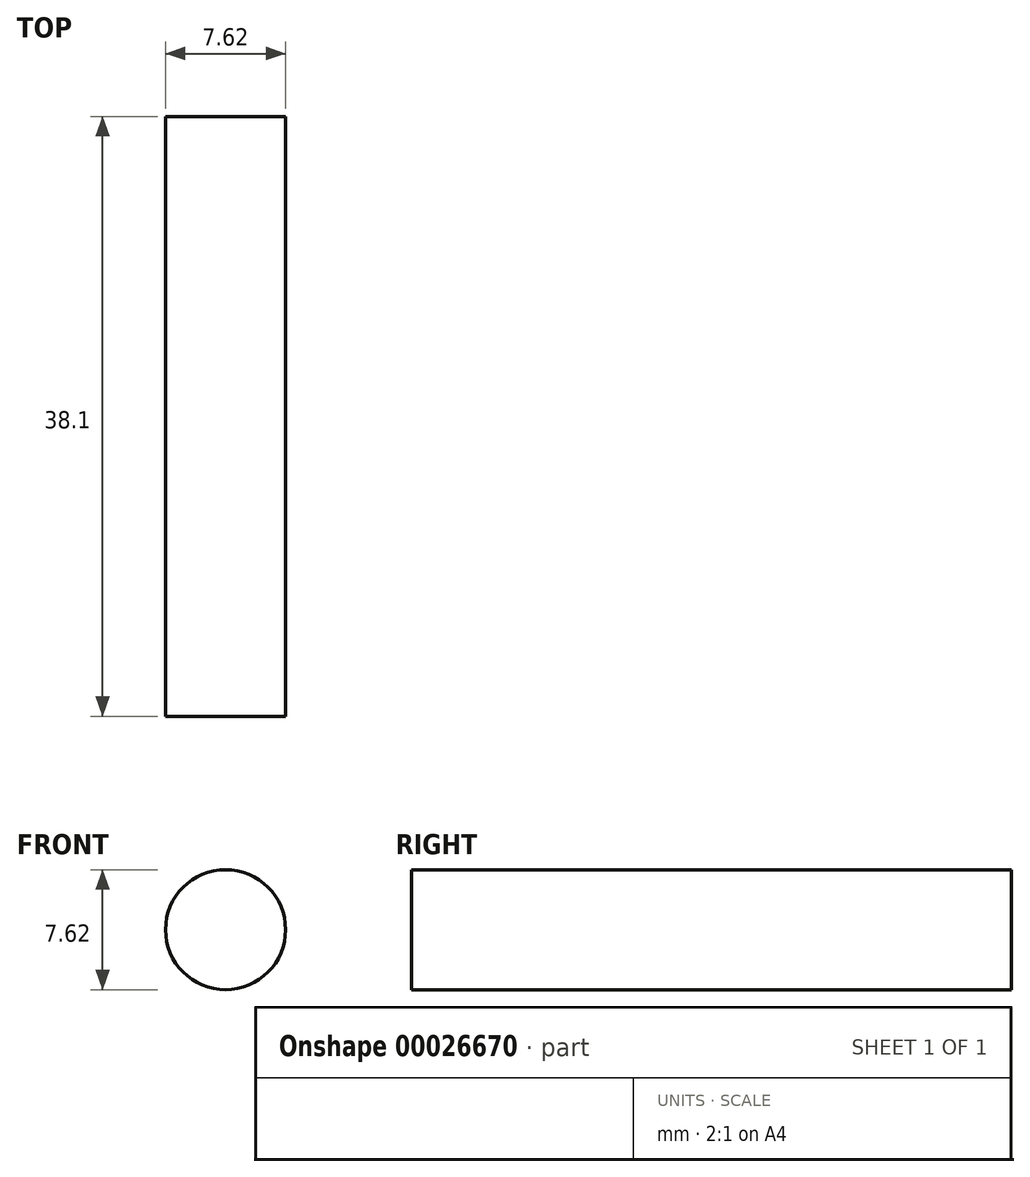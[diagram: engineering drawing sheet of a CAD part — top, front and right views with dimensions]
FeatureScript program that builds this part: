
annotation { "Feature Type Name" : "Feature", "Feature Type Description" : "" }
export const myFeature = defineFeature(function(context is Context, id is Id, definition is map)
    precondition{}
    {
        {
            var Q0;
            Q0=qCreatedBy(makeId("Front.planeOp"),FACE);
            var sketch = newSketch(context, id + "F0", { "sketchPlane" : qUnion([Q0])});
            skCircle(sketch, "E0", {"center": v(0, 0) * mm, "radius": 3.81 * mm});
            skSolve(sketch);
        }
        {
            var Q0;
            Q0 = qSketchRegion(id + "F0", true);
            extrude(context, id + "F1", {"entities" : qUnion([Q0]), "depth" : 38.1 * mm});
        }
    });
